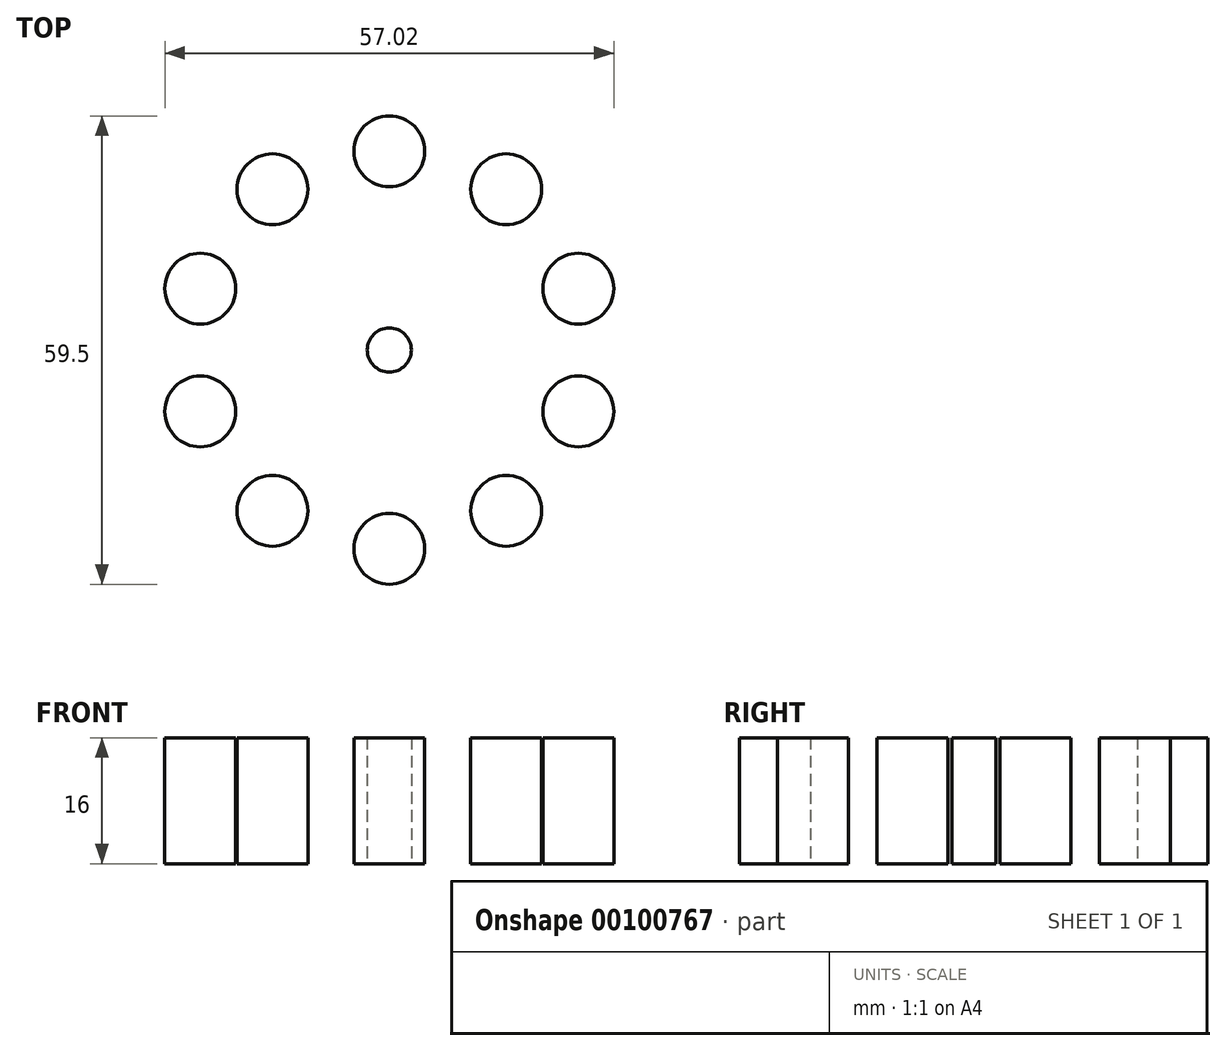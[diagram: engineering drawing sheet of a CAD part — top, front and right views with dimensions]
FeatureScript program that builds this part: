
annotation { "Feature Type Name" : "Feature", "Feature Type Description" : "" }
export const myFeature = defineFeature(function(context is Context, id is Id, definition is map)
    precondition{}
    {
        {
            var Q0;
            Q0=qCreatedBy(makeId("Top.planeOp"),FACE);
            var sketch = newSketch(context, id + "F0", { "sketchPlane" : qUnion([Q0])});
            skCircle(sketch, "E0", {"center": v(0, 0) * mm, "radius": 20.5 * mm, "construction": true});
            skCircle(sketch, "E1", {"center": v(0, 0) * mm, "radius": 30 * mm, "construction": true});
            skLineSegment(sketch, "E2", {"start": v(0, 20.5) * mm, "end": v(0, 30) * mm, "construction": true});
            skCircle(sketch, "E3", {"center": v(0, 25.25) * mm, "radius": 4.5 * mm});
            skCircle(sketch, "E4.1.0", {"center": v(-14.84, 20.43) * mm, "radius": 4.5 * mm});
            skCircle(sketch, "E4.2.0", {"center": v(-24.01, 7.8) * mm, "radius": 4.5 * mm});
            skCircle(sketch, "E4.3.0", {"center": v(-24.01, -7.8) * mm, "radius": 4.5 * mm});
            skCircle(sketch, "E4.4.0", {"center": v(-14.84, -20.43) * mm, "radius": 4.5 * mm});
            skCircle(sketch, "E4.5.0", {"center": v(0, -25.25) * mm, "radius": 4.5 * mm});
            skCircle(sketch, "E4.6.0", {"center": v(14.84, -20.43) * mm, "radius": 4.5 * mm});
            skCircle(sketch, "E4.7.0", {"center": v(24.01, -7.8) * mm, "radius": 4.5 * mm});
            skCircle(sketch, "E4.8.0", {"center": v(24.01, 7.8) * mm, "radius": 4.5 * mm});
            skCircle(sketch, "E4.9.0", {"center": v(14.84, 20.43) * mm, "radius": 4.5 * mm});
            skLineSegment(sketch, "E5", {"start": v(14.84, 20.43) * mm, "end": v(0, 0) * mm, "construction": true});
            skLineSegment(sketch, "E6", {"start": v(0, 0) * mm, "end": v(24.01, 7.8) * mm, "construction": true});
            skLineSegment(sketch, "E7", {"start": v(14.84, 20.43) * mm, "end": v(24.01, 7.8) * mm, "construction": true});
            skCircle(sketch, "E8", {"center": v(0, 0) * mm, "radius": 2.8 * mm});
            skSolve(sketch);
        }
        {
            var Q0;
            Q0=makeQuery(id+"F0.imprint","IMPRINT",FACE,{"disambiguationData":[TD([[makeQuery(id+"F0.imprint","IMPRINT",EDGE,{"derivedFrom":sQuery(id+"F0.wireOp",EDGE,"E4.1.0")}),1.0]])]});
            var Q1;
            Q1=makeQuery(id+"F0.imprint","IMPRINT",FACE,{"disambiguationData":[TD([[makeQuery(id+"F0.imprint","IMPRINT",EDGE,{"derivedFrom":sQuery(id+"F0.wireOp",EDGE,"E4.2.0")}),1.0]])]});
            var Q2;
            Q2=makeQuery(id+"F0.imprint","IMPRINT",FACE,{"disambiguationData":[TD([[makeQuery(id+"F0.imprint","IMPRINT",EDGE,{"derivedFrom":sQuery(id+"F0.wireOp",EDGE,"E4.3.0")}),1.0]])]});
            var Q3;
            Q3=makeQuery(id+"F0.imprint","IMPRINT",FACE,{"disambiguationData":[TD([[makeQuery(id+"F0.imprint","IMPRINT",EDGE,{"derivedFrom":sQuery(id+"F0.wireOp",EDGE,"E4.4.0")}),1.0]])]});
            var Q4;
            Q4=makeQuery(id+"F0.imprint","IMPRINT",FACE,{"disambiguationData":[TD([[makeQuery(id+"F0.imprint","IMPRINT",EDGE,{"derivedFrom":sQuery(id+"F0.wireOp",EDGE,"E4.5.0")}),1.0]])]});
            var Q5;
            Q5=makeQuery(id+"F0.imprint","IMPRINT",FACE,{"disambiguationData":[TD([[makeQuery(id+"F0.imprint","IMPRINT",EDGE,{"derivedFrom":sQuery(id+"F0.wireOp",EDGE,"E4.6.0")}),1.0]])]});
            var Q6;
            Q6=makeQuery(id+"F0.imprint","IMPRINT",FACE,{"disambiguationData":[TD([[makeQuery(id+"F0.imprint","IMPRINT",EDGE,{"derivedFrom":sQuery(id+"F0.wireOp",EDGE,"E4.7.0")}),1.0]])]});
            var Q7;
            Q7=makeQuery(id+"F0.imprint","IMPRINT",FACE,{"disambiguationData":[TD([[makeQuery(id+"F0.imprint","IMPRINT",EDGE,{"derivedFrom":sQuery(id+"F0.wireOp",EDGE,"E4.8.0")}),1.0]])]});
            var Q8;
            Q8=makeQuery(id+"F0.imprint","IMPRINT",FACE,{"disambiguationData":[TD([[makeQuery(id+"F0.imprint","IMPRINT",EDGE,{"derivedFrom":sQuery(id+"F0.wireOp",EDGE,"E4.9.0")}),1.0]])]});
            var Q9;
            Q9=makeQuery(id+"F0.imprint","IMPRINT",FACE,{"disambiguationData":[TD([[makeQuery(id+"F0.imprint","IMPRINT",EDGE,{"derivedFrom":sQuery(id+"F0.wireOp",EDGE,"E3")}),1.0]])]});
            var Q10;
            Q10=makeQuery(id+"F0.imprint","IMPRINT",FACE,{"disambiguationData":[TD([[makeQuery(id+"F0.imprint","IMPRINT",EDGE,{"derivedFrom":sQuery(id+"F0.wireOp",EDGE,"E8")}),1.0]])]});
            extrude(context, id + "F1", {"entities" : qUnion([Q0, Q1, Q2, Q3, Q4, Q5, Q6, Q7, Q8, Q9, Q10]), "depth" : 16 * mm});
        }
    });
